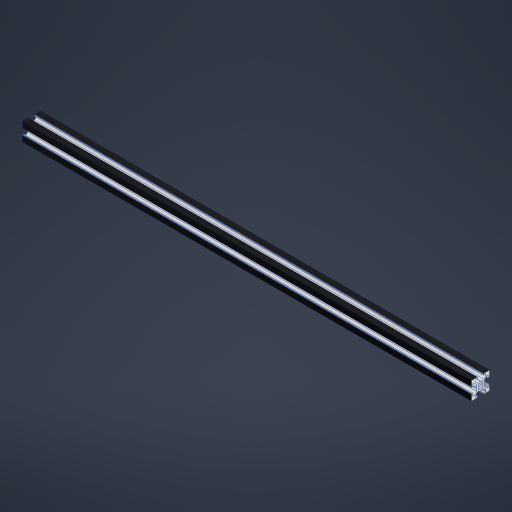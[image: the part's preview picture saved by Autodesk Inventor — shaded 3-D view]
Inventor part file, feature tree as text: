
AUTODESK INVENTOR PART (.ipt)
format: ipt  version: 2024.2 (Build 282272000, 272)  size: 348,672 bytes
history: native  units: mm
features: extrude x1, sketch x1
ambient origin geometry x8: Origin, YZ Plane, XZ Plane, XY Plane, X Axis, Y Axis, Z Axis, Center Point
bodies: Solid1 (feature_tree)
feature tree (2):
  extrude  "Extrusion1"  Depth=0.5mm
  sketch  "Sketch1"  dims[d2=6.5mm d3=0.5mm d4=4.0mm d5=3.465mm d6=5.48mm d7=0.795mm d8=0.305mm d9=2.95mm d11=0.75mm d14=45.0deg d15=10.0mm d16=1.0mm d17=3.0mm d18=45.0deg d19=40.0mm d21=360.0deg d23=500.0mm d24=0.0mm]
